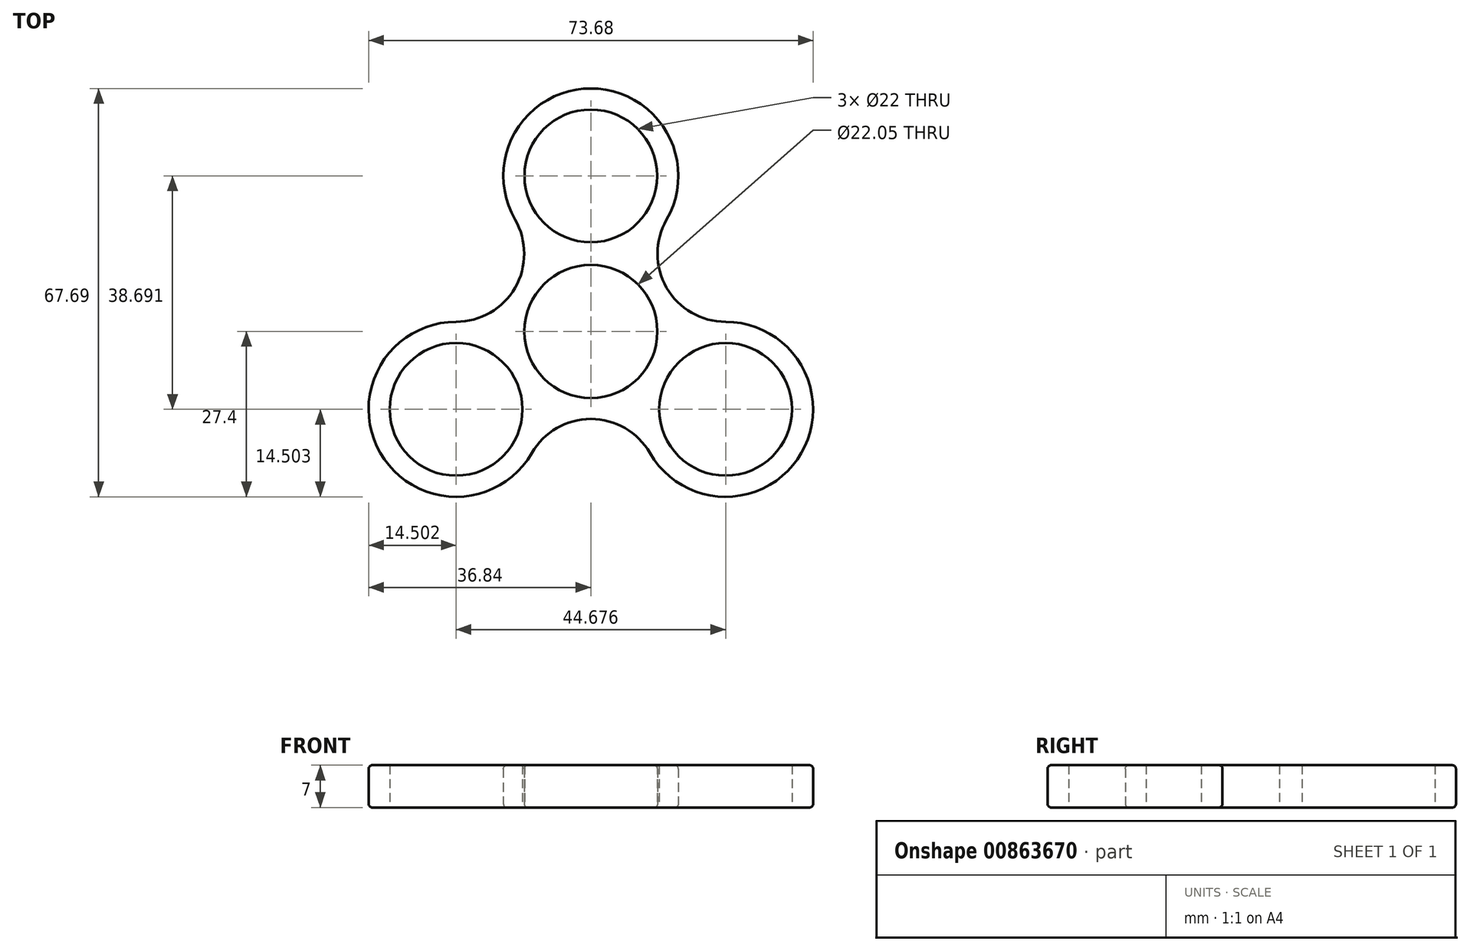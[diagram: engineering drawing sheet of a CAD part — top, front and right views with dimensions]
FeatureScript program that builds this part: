
annotation { "Feature Type Name" : "Feature", "Feature Type Description" : "" }
export const myFeature = defineFeature(function(context is Context, id is Id, definition is map)
    precondition{}
    {
        {
            var Q0;
            Q0=qCreatedBy(makeId("Top.planeOp"),FACE);
            var sketch = newSketch(context, id + "F0", { "sketchPlane" : qUnion([Q0])});
            skCircle(sketch, "E0", {"center": v(0, 0) * mm, "radius": 11.03 * mm});
            skCircle(sketch, "E1", {"center": v(0, 25.8) * mm, "radius": 11 * mm});
            skCircle(sketch, "E2", {"center": v(0, 25.8) * mm, "radius": 14.5 * mm, "construction": true});
            skLineSegment(sketch, "E3", {"start": v(0, 0) * mm, "end": v(-22.34, -12.9) * mm, "construction": true});
            skLineSegment(sketch, "E4", {"start": v(0, 0) * mm, "end": v(22.34, -12.9) * mm, "construction": true});
            skCircle(sketch, "E5", {"center": v(-22.34, -12.9) * mm, "radius": 14.5 * mm, "construction": true});
            skCircle(sketch, "E6", {"center": v(22.34, -12.9) * mm, "radius": 14.5 * mm, "construction": true});
            skCircle(sketch, "E7", {"center": v(0, 0) * mm, "radius": 40.3 * mm, "construction": true});
            skLineSegment(sketch, "E8.bottom", {"start": v(-40.3, -27.4) * mm, "end": v(40.3, -27.4) * mm, "construction": true});
            skLineSegment(sketch, "E8.top", {"start": v(-40.3, 40.3) * mm, "end": v(40.3, 40.3) * mm, "construction": true});
            skLineSegment(sketch, "E8.left", {"start": v(-40.3, -27.4) * mm, "end": v(-40.3, 40.3) * mm, "construction": true});
            skLineSegment(sketch, "E8.right", {"start": v(40.3, -27.4) * mm, "end": v(40.3, 40.3) * mm, "construction": true});
            skArc(sketch, "E9", {"start": v(12.56, 18.54) * mm, "mid": v(12.56, 7.25) * mm, "end": v(22.34, 1.6) * mm});
            skArc(sketch, "E10", {"start": v(12.56, 18.54) * mm, "mid": v(0, 40.3) * mm, "end": v(-12.56, 18.54) * mm});
            skLineSegment(sketch, "E11", {"start": v(12.56, 18.54) * mm, "end": v(-12.56, 18.54) * mm, "construction": true});
            skCircle(sketch, "E12.1.0", {"center": v(22.34, -12.9) * mm, "radius": 11 * mm});
            skArc(sketch, "E12.1.1", {"start": v(9.78, -20.15) * mm, "mid": v(0, -14.5) * mm, "end": v(-9.78, -20.15) * mm});
            skArc(sketch, "E12.1.2", {"start": v(9.78, -20.15) * mm, "mid": v(34.9, -20.15) * mm, "end": v(22.34, 1.6) * mm});
            skCircle(sketch, "E12.2.0", {"center": v(-22.34, -12.9) * mm, "radius": 11 * mm});
            skArc(sketch, "E12.2.1", {"start": v(-22.34, 1.6) * mm, "mid": v(-12.56, 7.25) * mm, "end": v(-12.56, 18.54) * mm});
            skArc(sketch, "E12.2.2", {"start": v(-22.34, 1.6) * mm, "mid": v(-34.9, -20.15) * mm, "end": v(-9.78, -20.15) * mm});
            skLineSegment(sketch, "E12.anchor1", {"start": v(0, 0) * mm, "end": v(0, 25.8) * mm, "construction": true});
            skLineSegment(sketch, "E13", {"start": v(0, 0) * mm, "end": v(-12.56, 7.25) * mm, "construction": true});
            skSolve(sketch);
        }
        {
            var Q0;
            Q0=makeQuery(id+"F0.imprint","IMPRINT",FACE,{"disambiguationData":[TD([[makeQuery(id+"F0.imprint","IMPRINT",EDGE,{"derivedFrom":sQuery(id+"F0.wireOp",EDGE,"E0")}),-1.0]])]});
            extrude(context, id + "F1", {"entities" : qUnion([Q0]), "depth" : 7 * mm, "offsetDistance" : 25.4 * mm});
        }
        {
            var Q0;
            Q0=makeQuery(id+"F1.opExtrude","CAP_EDGE",EDGE,{"disambiguationData":[OSD([sQuery(id+"F0.wireOp",EDGE,"E12.1.2")])],"isStart":false});
            var Q1;
            Q1=makeQuery(id+"F1.opExtrude","CAP_EDGE",EDGE,{"disambiguationData":[OSD([sQuery(id+"F0.wireOp",EDGE,"E12.1.1")])],"isStart":true});
            fillet(context, id + "F2", {"entities" : qUnion([Q0, Q1]), "radius" : 0.6 * mm, "tangentPropagation" : true, "defaultsChanged" : true, "vertexSettings" : [], "allowEdgeOverflow" : false});
        }
    });
